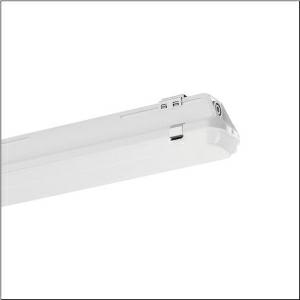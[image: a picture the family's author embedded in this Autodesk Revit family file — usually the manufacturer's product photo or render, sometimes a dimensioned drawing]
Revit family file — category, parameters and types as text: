
# Revit family: monsun_r__21_51fb107l420k005_9538
name_source: partatom
category: Lighting Fixtures
units: mm (PartAtom-declared; Revit-internal decimal feet)

## family parameters
Cut with Voids When Loaded = No
Host = Face
Light Source = No
Part Type = Normal
Room Calculation Point = No
Round Connector Dimension = Use Diameter
Shared = No

## types (1)
- Monsun® 21 (1 x LED, 2590 lm, 15.6 W, 4000K)
    Apparent Load = 16 VA
    CIE Flux Codes = 46 76 93 94 100
    Color Rendering = 80
    Color Temperature = 4000K
    Default Elevation = 1800 mm
    Description = Monsun® 21, damp-proof luminaire, chain hanger, primary optical cover: enclosure, of PMMA, light emission: direct distribution, primary light characteristic: symmetric, installation type: vertical mounting, horizontal mounting, surface-mounted, suspended mounting, LED, rated luminous flux: 2.590lm, luminous efficacy: 166lm/W, light colour: 840, colour temperature: 4000K, control gear: ON/OFF, with terminal, 3-pole, max. 2.5mm², through-wiring: 5x 2.5mm², mains connection: 220..240V, AC, 50/60Hz, rated input power: 16W, housing, of glass-fibre reinforced plastic, uncoated, bright grey, incl. chain hanger, length: 1.299mm, width: 90mm, height: 88mm, clip for enclosure, of stainless steel (V2A), ceiling mounting element, of stainless steel (V2A), chain hanger, of stainless steel (V2A), protection rating (complete): IP66, insulation class (complete): insulation class I (protective earthing), certification: CE, ENEC, VDE, UKCA, protection symbol: D, impact resistance: IK04, permissible operating ambient temperature: -25..+35°C, standard: EN 50419, EN 60598-2-1, corresponds to IFS (International Featured Standards) requirements for safety and quality in the food industry, for indoor or canopied outdoor use, no direct snow, no direct sun, no direct rain, LABS conformity tested according to VDMA 24364:2018-05, contact your sales advisor before using the luminaires in applications with unclear chemical exposure, large temperature fluctuations or condensation-forming humidity, packaging unit: 1 piece
    Height = 88 mm
    Lamp = 1 x LED
    Lamp Light Flux = 2590 lm
    Lamp Power = 15.6 W
    Lamp count = 1
    Length = 1299 mm
    Luminous efficacy = 166 lm/W
    Manufacturer = Siteco
    ModVariant = No
    Model = 51FB107L420K005
    Mounting Place = Ceiling
    Mounting Type = Surface mounted
    Number of Poles = 1
    OnlyDefault = Yes
    Power Factor = 1
    Product Name = Monsun® 21
    Product group = damp-proof luminaire
    ProductGroupID = 300
    Protection Class = Protection class I
    Protection Degree = IP 66
    RLX_Detail_Level = 1
    RLX_Emergency_Light_Flux = 0 lm
    RLX_Emergency_Type = 0
    RLX_Emergency_Type_DB = No
    RlxData = <blob elided: 89865 chars, md5=da72a46b>
    Socket = socket
    Standby Power = 0 W
    System Light Flux = 2590 lm
    System Power = 16 W
    Type Comments = Product without accessories
    Type Image = l_1319656.jpg
    URL = http://relux.com
    VarID = ---
    Voltage = 0 V
    Weight = 0.00 kg
    Width = 90 mm

## geometry (parser evidence)
native form markers: Blend x4, Sweep x14
no freeform markers — native parametric forms only
